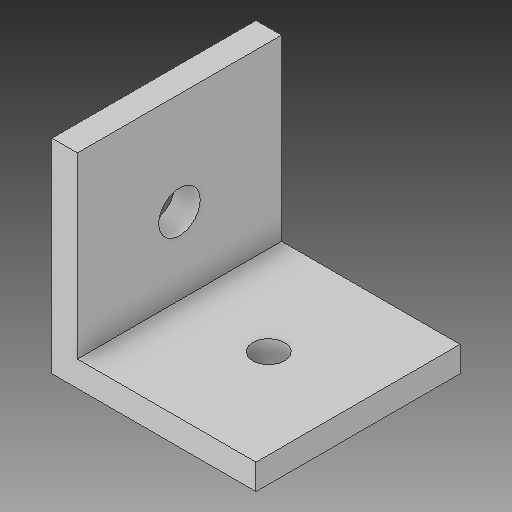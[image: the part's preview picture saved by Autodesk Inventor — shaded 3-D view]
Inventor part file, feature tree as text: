
AUTODESK INVENTOR PART (.ipt)
format: ipt  version: 2018 (Build 220112000, 112)  size: 115,200 bytes
history: native  units: in
note: dims shown in document units (in); Inventor stores cm internally (conversion verified against a paired STEP export)
features: extrude x3, sketch x3
ambient origin geometry x8: Origin, YZ Plane, XZ Plane, XY Plane, X Axis, Y Axis, Z Axis, Center Point
bodies: Solid1 (feature_tree)
feature tree (6):
  extrude  "Extrusion1"  Depth=1.0in
  extrude  "Extrusion2"  Depth=0.125in
  extrude  "Extrusion3"  Depth=1.0in
  sketch  "Sketch1"  dims[d0=0.125in d1=1.0in]
  sketch  "Sketch2"  dims[d2=1.0in d3=0.125in]
  sketch  "Sketch3"  dims[d4=1.0in d5=0.0in d6=0.5in d7=90.0deg d8=0.156in d9=1.0in d10=0.0in d11=0.2031in d12=1.0in d13=0.0in d14=0.5in]
